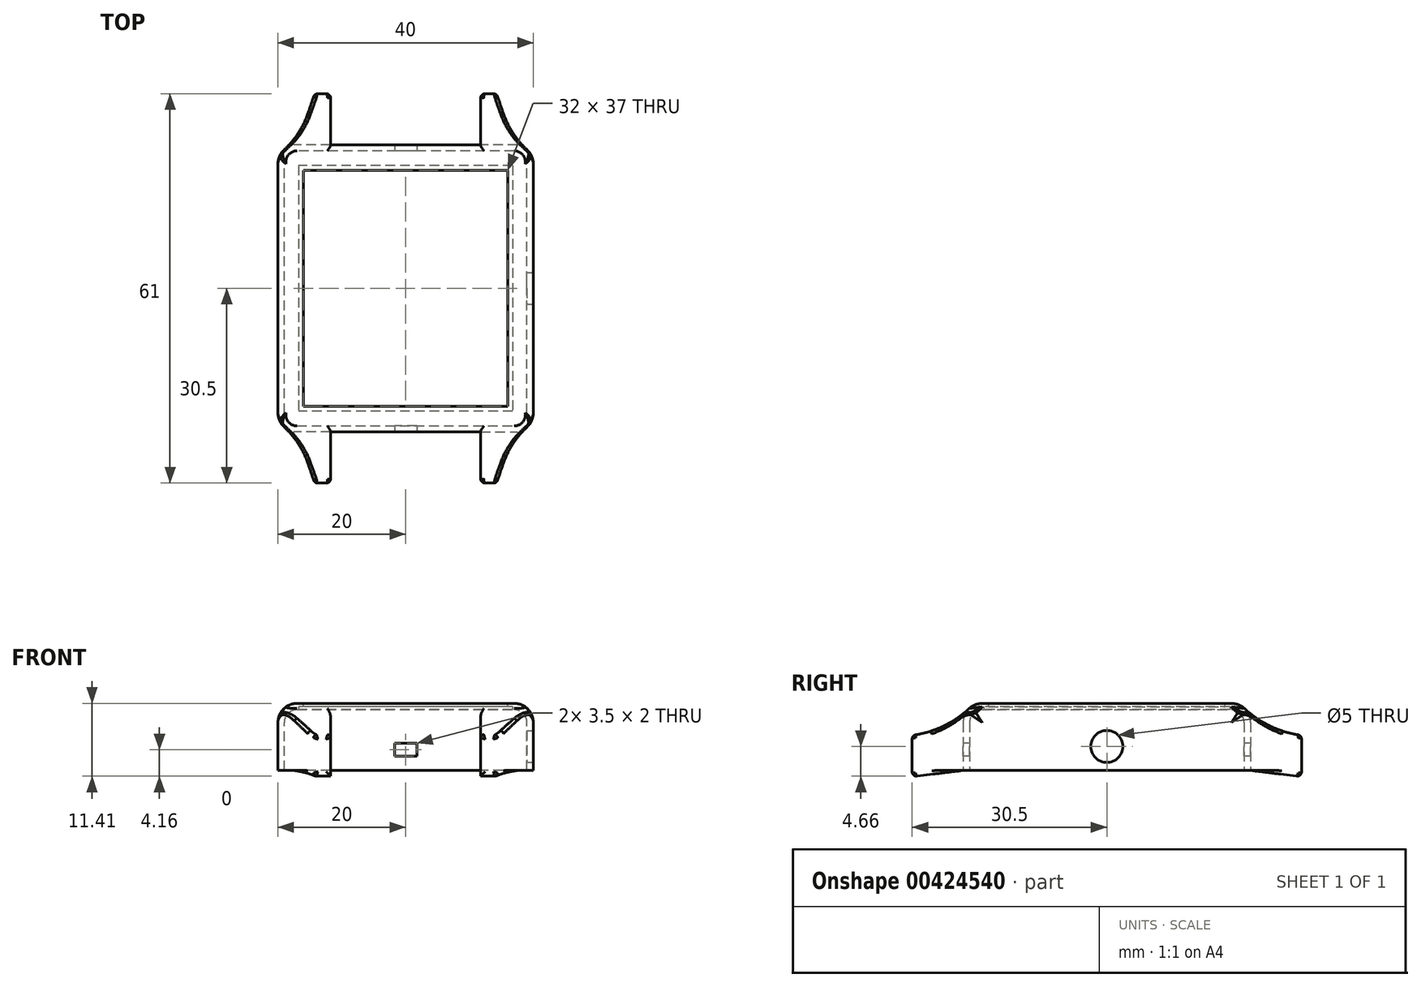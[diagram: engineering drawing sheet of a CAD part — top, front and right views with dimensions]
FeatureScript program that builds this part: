
annotation { "Feature Type Name" : "Feature", "Feature Type Description" : "" }
export const myFeature = defineFeature(function(context is Context, id is Id, definition is map)
    precondition{}
    {
        {
            var Q0;
            Q0=qCreatedBy(makeId("Top.planeOp"),FACE);
            var sketch = newSketch(context, id + "F0", { "sketchPlane" : qUnion([Q0])});
            skLineSegment(sketch, "E0.bottom", {"start": v(20, -22.5) * mm, "end": v(-20, -22.5) * mm});
            skLineSegment(sketch, "E0.top", {"start": v(20, 22.5) * mm, "end": v(-20, 22.5) * mm});
            skLineSegment(sketch, "E0.left", {"start": v(20, -22.5) * mm, "end": v(20, 22.5) * mm});
            skLineSegment(sketch, "E0.right", {"start": v(-20, -22.5) * mm, "end": v(-20, 22.5) * mm});
            skPoint(sketch, "E0.middle", {"position": v(0, 0) * mm});
            skSolve(sketch);
        }
        {
            var Q0;
            Q0=makeQuery(id+"F0.imprint","IMPRINT",FACE,{"disambiguationData":[TD([[makeQuery(id+"F0.imprint","IMPRINT",EDGE,{"derivedFrom":sQuery(id+"F0.wireOp",EDGE,"E0.bottom")}),-1.0]])]});
            extrude(context, id + "F1", {"entities" : qUnion([Q0]), "depth" : 10.5 * mm});
        }
        {
            var Q0;
            Q0=makeQuery(id+"F1.opExtrude","CAP_EDGE",EDGE,{"disambiguationData":[OSD([sQuery(id+"F0.wireOp",EDGE,"E0.bottom")])],"isStart":false});
            var Q1;
            Q1=makeQuery(id+"F1.opExtrude","CAP_EDGE",EDGE,{"disambiguationData":[OSD([sQuery(id+"F0.wireOp",EDGE,"E0.left")])],"isStart":false});
            var Q2;
            Q2=makeQuery(id+"F1.opExtrude","CAP_EDGE",EDGE,{"disambiguationData":[OSD([sQuery(id+"F0.wireOp",EDGE,"E0.right")])],"isStart":false});
            var Q3;
            Q3=makeQuery(id+"F1.opExtrude","CAP_EDGE",EDGE,{"disambiguationData":[OSD([sQuery(id+"F0.wireOp",EDGE,"E0.top")])],"isStart":false});
            var Q4;
            Q4=makeQuery(id+"F1.opExtrude","SWEPT_EDGE",EDGE,{"disambiguationData":[OSD([sQuery(id+"F0.wireOp",EDGE,"E0.top"),sQuery(id+"F0.wireOp",EDGE,"E0.left")])]});
            var Q5;
            Q5=makeQuery(id+"F1.opExtrude","SWEPT_EDGE",EDGE,{"disambiguationData":[OSD([sQuery(id+"F0.wireOp",EDGE,"E0.bottom"),sQuery(id+"F0.wireOp",EDGE,"E0.left")])]});
            var Q6;
            Q6=makeQuery(id+"F1.opExtrude","SWEPT_EDGE",EDGE,{"disambiguationData":[OSD([sQuery(id+"F0.wireOp",EDGE,"E0.bottom"),sQuery(id+"F0.wireOp",EDGE,"E0.right")])]});
            var Q7;
            Q7=makeQuery(id+"F1.opExtrude","SWEPT_EDGE",EDGE,{"disambiguationData":[OSD([sQuery(id+"F0.wireOp",EDGE,"E0.top"),sQuery(id+"F0.wireOp",EDGE,"E0.right")])]});
            fillet(context, id + "F2", {"entities" : qUnion([Q0, Q1, Q2, Q3, Q4, Q5, Q6, Q7]), "radius" : 3 * mm, "tangentPropagation" : true, "allowEdgeOverflow" : false});
        }
        {
            var Q0;
            Q0=makeQuery(id+"F1.opExtrude","CAP_FACE",FACE,{"disambiguationData":[OSD([sQuery(id+"F0.wireOp",EDGE,"E0.bottom"),sQuery(id+"F0.wireOp",EDGE,"E0.top"),sQuery(id+"F0.wireOp",EDGE,"E0.left"),sQuery(id+"F0.wireOp",EDGE,"E0.right")])],"isStart":true});
            shell(context, id + "F3", {"entities" : qUnion([Q0]), "thickness" : 1 * mm});
        }
        {
            var Q0;
            Q0=makeQuery(id+"F1.opExtrude","CAP_FACE",FACE,{"disambiguationData":[OSD([sQuery(id+"F0.wireOp",EDGE,"E0.bottom"),sQuery(id+"F0.wireOp",EDGE,"E0.top"),sQuery(id+"F0.wireOp",EDGE,"E0.left"),sQuery(id+"F0.wireOp",EDGE,"E0.right")])],"isStart":true});
            var sketch = newSketch(context, id + "F4", { "sketchPlane" : qUnion([Q0])});
            skLineSegment(sketch, "E1", {"start": v(0, 22.5) * mm, "end": v(0, -22.5) * mm});
            skLineSegment(sketch, "E2", {"start": v(-20, 0) * mm, "end": v(20, 0) * mm});
            skLineSegment(sketch, "E3", {"start": v(-17, 22.5) * mm, "end": v(-17, -22.5) * mm});
            skLineSegment(sketch, "E4", {"start": v(17, 22.5) * mm, "end": v(17, -22.5) * mm});
            skLineSegment(sketch, "E5", {"start": v(-11.75, 22.5) * mm, "end": v(-11.75, -22.5) * mm});
            skLineSegment(sketch, "E6", {"start": v(11.75, 22.5) * mm, "end": v(11.75, -22.5) * mm});
            skLineSegment(sketch, "E7", {"start": v(-11.75, -22.5) * mm, "end": v(-11.75, -30.5) * mm});
            skLineSegment(sketch, "E8", {"start": v(11.75, -22.5) * mm, "end": v(11.75, -30.5) * mm});
            skLineSegment(sketch, "E9", {"start": v(-11.75, -30.5) * mm, "end": v(-14.25, -30.5) * mm});
            skLineSegment(sketch, "E10", {"start": v(-14.25, -30.5) * mm, "end": v(-17, -22.5) * mm});
            skLineSegment(sketch, "E11", {"start": v(11.75, -30.5) * mm, "end": v(14.25, -30.5) * mm});
            skLineSegment(sketch, "E12", {"start": v(14.25, -30.5) * mm, "end": v(17, -22.5) * mm});
            skLineSegment(sketch, "E13", {"start": v(-11.75, 22.5) * mm, "end": v(-11.75, 30.5) * mm});
            skLineSegment(sketch, "E14", {"start": v(11.75, 22.5) * mm, "end": v(11.75, 30.5) * mm});
            skLineSegment(sketch, "E15", {"start": v(11.75, 30.5) * mm, "end": v(14.25, 30.5) * mm});
            skLineSegment(sketch, "E16", {"start": v(14.25, 30.5) * mm, "end": v(17, 22.5) * mm});
            skLineSegment(sketch, "E17", {"start": v(-11.75, 30.5) * mm, "end": v(-14.25, 30.5) * mm});
            skLineSegment(sketch, "E18", {"start": v(-14.25, 30.5) * mm, "end": v(-17, 22.5) * mm});
            skSolve(sketch);
        }
        {
            var Q0;
            {var subQ0=sQuery(id+"F4.wireOp",EDGE,"E13");Q0=makeQuery(id+"F4.imprint","IMPRINT",FACE,{"disambiguationData":[TD([[makeQuery(id+"F4.imprint","IMPRINT",EDGE,{"derivedFrom":subQ0}),1.0]])]});}
            var Q1;
            {var subQ0=sQuery(id+"F4.wireOp",EDGE,"E14");Q1=makeQuery(id+"F4.imprint","IMPRINT",FACE,{"disambiguationData":[TD([[makeQuery(id+"F4.imprint","IMPRINT",EDGE,{"derivedFrom":subQ0}),-1.0]])]});}
            var Q2;
            {var subQ0=sQuery(id+"F4.wireOp",EDGE,"E8");Q2=makeQuery(id+"F4.imprint","IMPRINT",FACE,{"disambiguationData":[TD([[makeQuery(id+"F4.imprint","IMPRINT",EDGE,{"derivedFrom":subQ0}),1.0]])]});}
            var Q3;
            {var subQ0=sQuery(id+"F4.wireOp",EDGE,"E7");Q3=makeQuery(id+"F4.imprint","IMPRINT",FACE,{"disambiguationData":[TD([[makeQuery(id+"F4.imprint","IMPRINT",EDGE,{"derivedFrom":subQ0}),-1.0]])]});}
            extrude(context, id + "F5", {"entities" : qUnion([Q0, Q1, Q2, Q3]), "operationType" : NewBodyOperationType.ADD, "oppositeDirection" : true, "depth" : 6.5 * mm});
        }
        {
            var Q0;
            {var subQ0=sQuery(id+"F4.wireOp",EDGE,"E13");Q0=makeQuery(id+"F4.imprint","IMPRINT",FACE,{"disambiguationData":[TD([[makeQuery(id+"F4.imprint","IMPRINT",EDGE,{"derivedFrom":subQ0}),1.0]])]});}
            extrude(context, id + "F6", {"entities" : qUnion([Q0]), "operationType" : NewBodyOperationType.ADD, "depth" : 1 * mm});
        }
        {
            var Q0;
            Q0=makeQuery(id+"F5.opExtrude","CAP_EDGE",EDGE,{"disambiguationData":[OSD([sQuery(id+"F4.wireOp",EDGE,"E17")])],"isStart":false});
            chamfer(context, id + "F7", {"entities" : qUnion([Q0]), "chamferType" : ChamferType.TWO_OFFSETS, "width1" : 1 * mm, "oppositeDirection" : false, "width2" : 8 * mm, "tangentPropagation" : true});
        }
        {
            var Q0;
            {var subQ0=sQuery(id+"F0.wireOp",EDGE,"E0.bottom");var subQ1=sQuery(id+"F0.wireOp",EDGE,"E0.top");Q0=makeQuery(id+"F5.boolean.opBoolean","MERGE",FACE,{"derivedFrom":[makeQuery(id+"F1.opExtrude","CAP_FACE",FACE,{"disambiguationData":[OSD([subQ0,subQ1,sQuery(id+"F0.wireOp",EDGE,"E0.left"),sQuery(id+"F0.wireOp",EDGE,"E0.right")])],"isStart":true}),makeQuery(id+"F5.opExtrude","CAP_FACE",FACE,{"disambiguationData":[OSD([subQ1,sQuery(id+"F4.wireOp",EDGE,"E7"),sQuery(id+"F4.wireOp",EDGE,"E9"),sQuery(id+"F4.wireOp",EDGE,"E10")])],"isStart":true}),makeQuery(id+"F5.opExtrude","CAP_FACE",FACE,{"disambiguationData":[OSD([subQ1,sQuery(id+"F4.wireOp",EDGE,"E8"),sQuery(id+"F4.wireOp",EDGE,"E11"),sQuery(id+"F4.wireOp",EDGE,"E12")])],"isStart":true}),makeQuery(id+"F5.opExtrude","CAP_FACE",FACE,{"disambiguationData":[OSD([subQ0,sQuery(id+"F4.wireOp",EDGE,"E13"),sQuery(id+"F4.wireOp",EDGE,"E17"),sQuery(id+"F4.wireOp",EDGE,"E18")])],"isStart":true}),makeQuery(id+"F5.opExtrude","CAP_FACE",FACE,{"disambiguationData":[OSD([subQ0,sQuery(id+"F4.wireOp",EDGE,"E14"),sQuery(id+"F4.wireOp",EDGE,"E15"),sQuery(id+"F4.wireOp",EDGE,"E16")])],"isStart":true})]});}
            var sketch = newSketch(context, id + "F8", { "sketchPlane" : qUnion([Q0])});
            skLineSegment(sketch, "E19", {"start": v(11.75, 22.5) * mm, "end": v(17, 22.5) * mm});
            skLineSegment(sketch, "E20", {"start": v(-11.75, -22.5) * mm, "end": v(-17, -22.5) * mm});
            skLineSegment(sketch, "E21", {"start": v(17, -22.5) * mm, "end": v(11.75, -22.5) * mm});
            skSolve(sketch);
        }
        {
            var Q0;
            Q0=makeQuery(id+"F8.imprint","IMPRINT",FACE,{"disambiguationData":[TD([[makeQuery(id+"F8.imprint","IMPRINT",EDGE,{"derivedFrom":sQuery(id+"F8.wireOp",EDGE,"E21")}),1.0]])]});
            var Q1;
            Q1=makeQuery(id+"F8.imprint","IMPRINT",FACE,{"disambiguationData":[TD([[makeQuery(id+"F8.imprint","IMPRINT",EDGE,{"derivedFrom":sQuery(id+"F8.wireOp",EDGE,"E20")}),1.0]])]});
            var Q2;
            Q2=makeQuery(id+"F8.imprint","IMPRINT",FACE,{"disambiguationData":[TD([[makeQuery(id+"F8.imprint","IMPRINT",EDGE,{"derivedFrom":sQuery(id+"F8.wireOp",EDGE,"E19")}),1.0]])]});
            extrude(context, id + "F9", {"entities" : qUnion([Q0, Q1, Q2]), "operationType" : NewBodyOperationType.ADD, "depth" : 1 * mm});
        }
        {
            var Q0;
            Q0=makeQuery(id+"F6.opExtrude","CAP_EDGE",EDGE,{"disambiguationData":[OSD([sQuery(id+"F0.wireOp",EDGE,"E0.bottom")])],"isStart":false});
            chamfer(context, id + "F10", {"entities" : qUnion([Q0]), "chamferType" : ChamferType.TWO_OFFSETS, "width1" : 1 * mm, "oppositeDirection" : false, "width2" : 8 * mm, "tangentPropagation" : true});
        }
        {
            var Q0;
            Q0=makeQuery(id+"F9.opExtrude","CAP_EDGE",EDGE,{"disambiguationData":[OSD([sQuery(id+"F8.wireOp",EDGE,"E21")])],"isStart":false});
            var Q1;
            Q1=makeQuery(id+"F9.opExtrude","CAP_EDGE",EDGE,{"disambiguationData":[OSD([sQuery(id+"F8.wireOp",EDGE,"E20")])],"isStart":false});
            chamfer(context, id + "F11", {"entities" : qUnion([Q0, Q1]), "chamferType" : ChamferType.TWO_OFFSETS, "width1" : 8 * mm, "oppositeDirection" : false, "width2" : 1 * mm, "tangentPropagation" : true});
        }
        {
            var Q0;
            Q0=makeQuery(id+"F9.opExtrude","CAP_EDGE",EDGE,{"disambiguationData":[OSD([sQuery(id+"F8.wireOp",EDGE,"E19")])],"isStart":false});
            chamfer(context, id + "F12", {"entities" : qUnion([Q0]), "chamferType" : ChamferType.TWO_OFFSETS, "width1" : 1 * mm, "oppositeDirection" : true, "width2" : 8 * mm, "tangentPropagation" : true});
        }
        {
            var Q0;
            Q0=makeQuery(id+"F5.opExtrude","CAP_EDGE",EDGE,{"disambiguationData":[OSD([sQuery(id+"F4.wireOp",EDGE,"E11")])],"isStart":false});
            chamfer(context, id + "F13", {"entities" : qUnion([Q0]), "chamferType" : ChamferType.TWO_OFFSETS, "width1" : 1 * mm, "oppositeDirection" : false, "width2" : 8 * mm});
        }
        {
            var Q0;
            Q0=makeQuery(id+"F5.opExtrude","CAP_EDGE",EDGE,{"disambiguationData":[OSD([sQuery(id+"F4.wireOp",EDGE,"E15")])],"isStart":false});
            chamfer(context, id + "F14", {"entities" : qUnion([Q0]), "chamferType" : ChamferType.TWO_OFFSETS, "width1" : 1 * mm, "oppositeDirection" : true, "width2" : 8 * mm, "tangentPropagation" : true});
        }
        {
            var Q0;
            Q0=makeQuery(id+"F5.opExtrude","CAP_EDGE",EDGE,{"disambiguationData":[OSD([sQuery(id+"F4.wireOp",EDGE,"E9")])],"isStart":false});
            chamfer(context, id + "F15", {"entities" : qUnion([Q0]), "chamferType" : ChamferType.TWO_OFFSETS, "width1" : 1 * mm, "oppositeDirection" : true, "width2" : 8 * mm, "tangentPropagation" : true});
        }
        {
            var Q0;
            Q0=makeQuery(id+"F1.opExtrude","SWEPT_FACE",FACE,{"disambiguationData":[OSD([sQuery(id+"F0.wireOp",EDGE,"E0.bottom")])]});
            var sketch = newSketch(context, id + "F16", { "sketchPlane" : qUnion([Q0])});
            skLineSegment(sketch, "E22", {"start": v(-11.75, 3.25) * mm, "end": v(11.75, 3.25) * mm});
            skLineSegment(sketch, "E23", {"start": v(0, 0) * mm, "end": v(0, 7.5) * mm});
            skLineSegment(sketch, "E24.bottom", {"start": v(1.75, 2.25) * mm, "end": v(-1.75, 2.25) * mm});
            skLineSegment(sketch, "E24.top", {"start": v(1.75, 4.25) * mm, "end": v(-1.75, 4.25) * mm});
            skLineSegment(sketch, "E24.left", {"start": v(1.75, 2.25) * mm, "end": v(1.75, 4.25) * mm});
            skLineSegment(sketch, "E24.right", {"start": v(-1.75, 2.25) * mm, "end": v(-1.75, 4.25) * mm});
            skPoint(sketch, "E24.middle", {"position": v(0, 3.25) * mm});
            skSolve(sketch);
        }
        {
            var Q0;
            {var subQ0=sQuery(id+"F16.wireOp",EDGE,"E24.right");var subQ1=sQuery(id+"F16.wireOp",EDGE,"E22");var subQ2=makeQuery(id+"F16.imprint","INTERSECT",VERTEX,{"derivedFrom":[subQ1,subQ0]});Q0=makeQuery(id+"F16.imprint","IMPRINT",FACE,{"disambiguationData":[TD([[makeQuery(id+"F16.imprint","IMPRINT",EDGE,{"disambiguationData":[TD([[subQ2,-1.0]])],"derivedFrom":subQ1}),1.0]])]});}
            var Q1;
            {var subQ0=sQuery(id+"F16.wireOp",EDGE,"E23");var subQ1=sQuery(id+"F16.wireOp",EDGE,"E22");var subQ2=makeQuery(id+"F16.imprint","INTERSECT",VERTEX,{"derivedFrom":[subQ1,subQ0]});Q1=makeQuery(id+"F16.imprint","IMPRINT",FACE,{"disambiguationData":[TD([[makeQuery(id+"F16.imprint","IMPRINT",EDGE,{"disambiguationData":[TD([[subQ2,-1.0]])],"derivedFrom":subQ1}),1.0]])]});}
            var Q2;
            {var subQ0=sQuery(id+"F16.wireOp",EDGE,"E23");var subQ1=sQuery(id+"F16.wireOp",EDGE,"E22");var subQ2=makeQuery(id+"F16.imprint","INTERSECT",VERTEX,{"derivedFrom":[subQ1,subQ0]});Q2=makeQuery(id+"F16.imprint","IMPRINT",FACE,{"disambiguationData":[TD([[makeQuery(id+"F16.imprint","IMPRINT",EDGE,{"disambiguationData":[TD([[subQ2,-1.0]])],"derivedFrom":subQ1}),-1.0]])]});}
            var Q3;
            {var subQ0=sQuery(id+"F16.wireOp",EDGE,"E24.right");var subQ1=sQuery(id+"F16.wireOp",EDGE,"E22");var subQ2=makeQuery(id+"F16.imprint","INTERSECT",VERTEX,{"derivedFrom":[subQ1,subQ0]});Q3=makeQuery(id+"F16.imprint","IMPRINT",FACE,{"disambiguationData":[TD([[makeQuery(id+"F16.imprint","IMPRINT",EDGE,{"disambiguationData":[TD([[subQ2,-1.0]])],"derivedFrom":subQ1}),-1.0]])]});}
            extrude(context, id + "F17", {"entities" : qUnion([Q0, Q1, Q2, Q3]), "operationType" : NewBodyOperationType.REMOVE, "oppositeDirection" : true, "depth" : 50 * mm});
        }
        {
            var Q0;
            Q0=makeQuery(id+"F1.opExtrude","SWEPT_FACE",FACE,{"disambiguationData":[OSD([sQuery(id+"F0.wireOp",EDGE,"E0.left")])]});
            var sketch = newSketch(context, id + "F18", { "sketchPlane" : qUnion([Q0])});
            skLineSegment(sketch, "E25", {"start": v(19.5, 3.75) * mm, "end": v(-19.5, 3.75) * mm});
            skLineSegment(sketch, "E26", {"start": v(0, 7.5) * mm, "end": v(0, 0) * mm});
            skCircle(sketch, "E27", {"center": v(0, 3.75) * mm, "radius": 2.5 * mm});
            skSolve(sketch);
        }
        {
            var Q0;
            {var subQ0=sQuery(id+"F18.wireOp",EDGE,"E26");var subQ1=sQuery(id+"F18.wireOp",EDGE,"E25");var subQ2=makeQuery(id+"F18.imprint","INTERSECT",VERTEX,{"derivedFrom":[subQ1,subQ0]});Q0=makeQuery(id+"F18.imprint","IMPRINT",FACE,{"disambiguationData":[TD([[makeQuery(id+"F18.imprint","IMPRINT",EDGE,{"disambiguationData":[TD([[subQ2,-1.0]])],"derivedFrom":subQ1}),-1.0]])]});}
            var Q1;
            {var subQ0=sQuery(id+"F18.wireOp",EDGE,"E27");var subQ1=sQuery(id+"F18.wireOp",EDGE,"E25");var subQ2=makeQuery(id+"F18.imprint","INTERSECT",VERTEX,{"disambiguationData":[OD(0.0)],"derivedFrom":[subQ1,subQ0]});Q1=makeQuery(id+"F18.imprint","IMPRINT",FACE,{"disambiguationData":[TD([[makeQuery(id+"F18.imprint","IMPRINT",EDGE,{"disambiguationData":[TD([[subQ2,-1.0]])],"derivedFrom":subQ1}),-1.0]])]});}
            var Q2;
            {var subQ0=sQuery(id+"F18.wireOp",EDGE,"E27");var subQ1=sQuery(id+"F18.wireOp",EDGE,"E25");var subQ2=makeQuery(id+"F18.imprint","INTERSECT",VERTEX,{"disambiguationData":[OD(0.0)],"derivedFrom":[subQ1,subQ0]});Q2=makeQuery(id+"F18.imprint","IMPRINT",FACE,{"disambiguationData":[TD([[makeQuery(id+"F18.imprint","IMPRINT",EDGE,{"disambiguationData":[TD([[subQ2,-1.0]])],"derivedFrom":subQ1}),1.0]])]});}
            var Q3;
            {var subQ0=sQuery(id+"F18.wireOp",EDGE,"E26");var subQ1=sQuery(id+"F18.wireOp",EDGE,"E25");var subQ2=makeQuery(id+"F18.imprint","INTERSECT",VERTEX,{"derivedFrom":[subQ1,subQ0]});Q3=makeQuery(id+"F18.imprint","IMPRINT",FACE,{"disambiguationData":[TD([[makeQuery(id+"F18.imprint","IMPRINT",EDGE,{"disambiguationData":[TD([[subQ2,-1.0]])],"derivedFrom":subQ1}),1.0]])]});}
            extrude(context, id + "F19", {"entities" : qUnion([Q0, Q1, Q2, Q3]), "operationType" : NewBodyOperationType.REMOVE, "oppositeDirection" : true, "depth" : 10 * mm});
        }
        {
            var Q0;
            Q0=makeQuery(id+"F1.opExtrude","CAP_FACE",FACE,{"disambiguationData":[OSD([sQuery(id+"F0.wireOp",EDGE,"E0.bottom"),sQuery(id+"F0.wireOp",EDGE,"E0.top"),sQuery(id+"F0.wireOp",EDGE,"E0.left"),sQuery(id+"F0.wireOp",EDGE,"E0.right")])],"isStart":false});
            var sketch = newSketch(context, id + "F20", { "sketchPlane" : qUnion([Q0])});
            skLineSegment(sketch, "E28.bottom", {"start": v(16, -18.5) * mm, "end": v(-16, -18.5) * mm});
            skLineSegment(sketch, "E28.top", {"start": v(16, 18.5) * mm, "end": v(-16, 18.5) * mm});
            skLineSegment(sketch, "E28.left", {"start": v(16, -18.5) * mm, "end": v(16, 18.5) * mm});
            skLineSegment(sketch, "E28.right", {"start": v(-16, -18.5) * mm, "end": v(-16, 18.5) * mm});
            skPoint(sketch, "E28.middle", {"position": v(0, 0) * mm});
            skSolve(sketch);
        }
        {
            var Q0;
            Q0=makeQuery(id+"F20.imprint","IMPRINT",FACE,{"disambiguationData":[TD([[makeQuery(id+"F20.imprint","IMPRINT",EDGE,{"derivedFrom":sQuery(id+"F20.wireOp",EDGE,"E28.bottom")}),-1.0]])]});
            extrude(context, id + "F21", {"entities" : qUnion([Q0]), "operationType" : NewBodyOperationType.REMOVE, "oppositeDirection" : true, "depth" : 25 * mm});
        }
        {
            var Q0;
            Q0=makeQuery(id+"F3.opShell","OFFSET_FACE",FACE,{"disambiguationData":[OSD([sQuery(id+"F0.wireOp",EDGE,"E0.bottom"),sQuery(id+"F0.wireOp",EDGE,"E0.top"),sQuery(id+"F0.wireOp",EDGE,"E0.left"),sQuery(id+"F0.wireOp",EDGE,"E0.right")])]});
            var sketch = newSketch(context, id + "F22", { "sketchPlane" : qUnion([Q0])});
            skLineSegment(sketch, "E29.bottom", {"start": v(16.75, -19.25) * mm, "end": v(-16.75, -19.25) * mm});
            skLineSegment(sketch, "E29.top", {"start": v(16.75, 19.25) * mm, "end": v(-16.75, 19.25) * mm});
            skLineSegment(sketch, "E29.left", {"start": v(16.75, -19.25) * mm, "end": v(16.75, 19.25) * mm});
            skLineSegment(sketch, "E29.right", {"start": v(-16.75, -19.25) * mm, "end": v(-16.75, 19.25) * mm});
            skPoint(sketch, "E29.middle", {"position": v(0, 0) * mm});
            skSolve(sketch);
        }
        {
            var Q0;
            Q0=makeQuery(id+"F22.imprint","IMPRINT",FACE,{"disambiguationData":[TD([[makeQuery(id+"F22.imprint","IMPRINT",EDGE,{"derivedFrom":sQuery(id+"F22.wireOp",EDGE,"E29.bottom")}),-1.0]])]});
            extrude(context, id + "F23", {"entities" : qUnion([Q0]), "operationType" : NewBodyOperationType.REMOVE, "oppositeDirection" : true, "depth" : .5 * mm});
        }
        {
            var Q0;
            {var subQ0=sQuery(id+"F0.wireOp",EDGE,"E0.right");var subQ1=sQuery(id+"F0.wireOp",EDGE,"E0.bottom");Q0=makeQuery(id+"F5.boolean.opBoolean","MERGE",EDGE,{"derivedFrom":[makeQuery(id+"F2.opFillet","BLEND_EDGE",EDGE,{"blendedFrom":[makeQuery(id+"F1.opExtrude","SWEPT_EDGE",EDGE,{"disambiguationData":[OSD([subQ1,subQ0])]}),makeQuery(id+"F1.opExtrude","SWEPT_FACE",FACE,{"disambiguationData":[OSD([subQ1])]})],"blendedInto":[makeQuery(id+"F1.opExtrude","SWEPT_FACE",FACE,{"disambiguationData":[OSD([subQ1])]})]}),makeQuery(id+"F5.opExtrude","SWEPT_EDGE",EDGE,{"disambiguationData":[OSD([subQ1,sQuery(id+"F0.wireOp",EDGE,"E0.top"),sQuery(id+"F0.wireOp",EDGE,"E0.left"),subQ0,sQuery(id+"F4.wireOp",EDGE,"E3"),sQuery(id+"F4.wireOp",EDGE,"E18")])]})]});}
            var Q1;
            {var subQ0=sQuery(id+"F0.wireOp",EDGE,"E0.left");var subQ1=sQuery(id+"F0.wireOp",EDGE,"E0.bottom");Q1=makeQuery(id+"F5.boolean.opBoolean","MERGE",EDGE,{"derivedFrom":[makeQuery(id+"F2.opFillet","BLEND_EDGE",EDGE,{"blendedFrom":[makeQuery(id+"F1.opExtrude","SWEPT_EDGE",EDGE,{"disambiguationData":[OSD([subQ1,subQ0])]}),makeQuery(id+"F1.opExtrude","SWEPT_FACE",FACE,{"disambiguationData":[OSD([subQ1])]})],"blendedInto":[makeQuery(id+"F1.opExtrude","SWEPT_FACE",FACE,{"disambiguationData":[OSD([subQ1])]})]}),makeQuery(id+"F5.opExtrude","SWEPT_EDGE",EDGE,{"disambiguationData":[OSD([subQ1,sQuery(id+"F0.wireOp",EDGE,"E0.top"),subQ0,sQuery(id+"F0.wireOp",EDGE,"E0.right"),sQuery(id+"F4.wireOp",EDGE,"E4"),sQuery(id+"F4.wireOp",EDGE,"E16")])]})]});}
            var Q2;
            {var subQ0=sQuery(id+"F0.wireOp",EDGE,"E0.right");var subQ1=sQuery(id+"F0.wireOp",EDGE,"E0.top");Q2=makeQuery(id+"F5.boolean.opBoolean","MERGE",EDGE,{"derivedFrom":[makeQuery(id+"F2.opFillet","BLEND_EDGE",EDGE,{"blendedFrom":[makeQuery(id+"F1.opExtrude","SWEPT_EDGE",EDGE,{"disambiguationData":[OSD([subQ1,subQ0])]}),makeQuery(id+"F1.opExtrude","SWEPT_FACE",FACE,{"disambiguationData":[OSD([subQ1])]})],"blendedInto":[makeQuery(id+"F1.opExtrude","SWEPT_FACE",FACE,{"disambiguationData":[OSD([subQ1])]})]}),makeQuery(id+"F5.opExtrude","SWEPT_EDGE",EDGE,{"disambiguationData":[OSD([sQuery(id+"F0.wireOp",EDGE,"E0.bottom"),subQ1,sQuery(id+"F0.wireOp",EDGE,"E0.left"),subQ0,sQuery(id+"F4.wireOp",EDGE,"E3"),sQuery(id+"F4.wireOp",EDGE,"E10")])]})]});}
            var Q3;
            {var subQ0=sQuery(id+"F0.wireOp",EDGE,"E0.left");var subQ1=sQuery(id+"F0.wireOp",EDGE,"E0.top");Q3=makeQuery(id+"F5.boolean.opBoolean","MERGE",EDGE,{"derivedFrom":[makeQuery(id+"F2.opFillet","BLEND_EDGE",EDGE,{"blendedFrom":[makeQuery(id+"F1.opExtrude","SWEPT_EDGE",EDGE,{"disambiguationData":[OSD([subQ1,subQ0])]}),makeQuery(id+"F1.opExtrude","SWEPT_FACE",FACE,{"disambiguationData":[OSD([subQ1])]})],"blendedInto":[makeQuery(id+"F1.opExtrude","SWEPT_FACE",FACE,{"disambiguationData":[OSD([subQ1])]})]}),makeQuery(id+"F5.opExtrude","SWEPT_EDGE",EDGE,{"disambiguationData":[OSD([sQuery(id+"F0.wireOp",EDGE,"E0.bottom"),subQ1,subQ0,sQuery(id+"F0.wireOp",EDGE,"E0.right"),sQuery(id+"F4.wireOp",EDGE,"E4"),sQuery(id+"F4.wireOp",EDGE,"E12")])]})]});}
            fillet(context, id + "F24", {"entities" : qUnion([Q0, Q1, Q2, Q3]), "radius" : 14 * mm, "tangentPropagation" : true, "allowEdgeOverflow" : false});
        }
        {
            var Q0;
            Q0=makeQuery(id+"F13.opChamfer","BLEND_EDGE",EDGE,{"blendedFrom":[makeQuery(id+"F5.opExtrude","CAP_EDGE",EDGE,{"disambiguationData":[OSD([sQuery(id+"F4.wireOp",EDGE,"E11")])],"isStart":false}),makeQuery(id+"F1.opExtrude","SWEPT_FACE",FACE,{"disambiguationData":[OSD([sQuery(id+"F0.wireOp",EDGE,"E0.top")])]})],"blendedInto":[makeQuery(id+"F1.opExtrude","SWEPT_FACE",FACE,{"disambiguationData":[OSD([sQuery(id+"F0.wireOp",EDGE,"E0.top")])]})]});
            var Q1;
            Q1=makeQuery(id+"F14.opChamfer","BLEND_EDGE",EDGE,{"blendedFrom":[makeQuery(id+"F5.opExtrude","CAP_EDGE",EDGE,{"disambiguationData":[OSD([sQuery(id+"F4.wireOp",EDGE,"E15")])],"isStart":false}),makeQuery(id+"F1.opExtrude","SWEPT_FACE",FACE,{"disambiguationData":[OSD([sQuery(id+"F0.wireOp",EDGE,"E0.bottom")])]})],"blendedInto":[makeQuery(id+"F1.opExtrude","SWEPT_FACE",FACE,{"disambiguationData":[OSD([sQuery(id+"F0.wireOp",EDGE,"E0.bottom")])]})]});
            var Q2;
            Q2=makeQuery(id+"F7.opChamfer","BLEND_EDGE",EDGE,{"blendedFrom":[makeQuery(id+"F5.opExtrude","CAP_EDGE",EDGE,{"disambiguationData":[OSD([sQuery(id+"F4.wireOp",EDGE,"E17")])],"isStart":false}),makeQuery(id+"F1.opExtrude","SWEPT_FACE",FACE,{"disambiguationData":[OSD([sQuery(id+"F0.wireOp",EDGE,"E0.bottom")])]})],"blendedInto":[makeQuery(id+"F1.opExtrude","SWEPT_FACE",FACE,{"disambiguationData":[OSD([sQuery(id+"F0.wireOp",EDGE,"E0.bottom")])]})]});
            var Q3;
            Q3=makeQuery(id+"F15.opChamfer","BLEND_EDGE",EDGE,{"blendedFrom":[makeQuery(id+"F5.opExtrude","CAP_EDGE",EDGE,{"disambiguationData":[OSD([sQuery(id+"F4.wireOp",EDGE,"E9")])],"isStart":false}),makeQuery(id+"F1.opExtrude","SWEPT_FACE",FACE,{"disambiguationData":[OSD([sQuery(id+"F0.wireOp",EDGE,"E0.top")])]})],"blendedInto":[makeQuery(id+"F1.opExtrude","SWEPT_FACE",FACE,{"disambiguationData":[OSD([sQuery(id+"F0.wireOp",EDGE,"E0.top")])]})]});
            var Q4;
            {var subQ0=sQuery(id+"F4.wireOp",EDGE,"E10");var subQ1=sQuery(id+"F0.wireOp",EDGE,"E0.top");var subQ2=sQuery(id+"F0.wireOp",EDGE,"E0.right");Q4=makeQuery(id+"F24.opFillet","TWEAK_EDGE",EDGE,{"derivedFrom":[makeQuery(id+"F15.opChamfer","BLEND_VERTEX",VERTEX,{"blendedFrom":[makeQuery(id+"F5.opExtrude","CAP_EDGE",EDGE,{"disambiguationData":[OSD([sQuery(id+"F4.wireOp",EDGE,"E9")])],"isStart":false}),makeQuery(id+"F2.opFillet","BLEND_FACE",FACE,{"disambiguationData":[OSD([subQ1,subQ2]),TDD([makeQuery(id+"F1.opExtrude","SWEPT_EDGE",EDGE,{"disambiguationData":[OSD([subQ1,subQ2])]})])]}),makeQuery(id+"F1.opExtrude","SWEPT_FACE",FACE,{"disambiguationData":[OSD([subQ1])]}),makeQuery(id+"F9.boolean.opBoolean","MERGE",FACE,{"derivedFrom":[makeQuery(id+"F5.opExtrude","SWEPT_FACE",FACE,{"disambiguationData":[OSD([subQ0])]}),makeQuery(id+"F9.opExtrude","SWEPT_FACE",FACE,{"disambiguationData":[OSD([subQ0])]})]})],"blendedInto":[makeQuery(id+"F2.opFillet","BLEND_FACE",FACE,{"disambiguationData":[OSD([subQ1,subQ2]),TDD([makeQuery(id+"F1.opExtrude","SWEPT_EDGE",EDGE,{"disambiguationData":[OSD([subQ1,subQ2])]})])]}),makeQuery(id+"F1.opExtrude","SWEPT_FACE",FACE,{"disambiguationData":[OSD([subQ1])]}),makeQuery(id+"F9.boolean.opBoolean","MERGE",FACE,{"derivedFrom":[makeQuery(id+"F5.opExtrude","SWEPT_FACE",FACE,{"disambiguationData":[OSD([subQ0])]}),makeQuery(id+"F9.opExtrude","SWEPT_FACE",FACE,{"disambiguationData":[OSD([subQ0])]})]})]})]});}
            fillet(context, id + "F25", {"entities" : qUnion([Q0, Q1, Q2, Q3, Q4]), "radius" : 16 * mm, "tangentPropagation" : true, "allowEdgeOverflow" : false});
        }
        {
            var Q0;
            {var subQ0=sQuery(id+"F0.wireOp",EDGE,"E0.right");var subQ1=sQuery(id+"F0.wireOp",EDGE,"E0.top");Q0=makeQuery(id+"F25.opFillet","TWEAK_EDGE",EDGE,{"derivedFrom":[makeQuery(id+"F2.opFillet","BLEND_VERTEX",VERTEX,{"blendedFrom":[makeQuery(id+"F1.opExtrude","CAP_VERTEX",VERTEX,{"disambiguationData":[OSD([subQ1,subQ0])],"isStart":false}),makeQuery(id+"F1.opExtrude","SWEPT_EDGE",EDGE,{"disambiguationData":[OSD([subQ1,subQ0])]}),makeQuery(id+"F1.opExtrude","CAP_EDGE",EDGE,{"disambiguationData":[OSD([subQ0])],"isStart":false}),makeQuery(id+"F1.opExtrude","SWEPT_FACE",FACE,{"disambiguationData":[OSD([subQ0])]})],"blendedInto":[makeQuery(id+"F1.opExtrude","SWEPT_FACE",FACE,{"disambiguationData":[OSD([subQ0])]})]})]});}
            var Q1;
            Q1=makeQuery(id+"F25.opFillet","BLEND_EDGE",EDGE,{"blendedFrom":[makeQuery(id+"F15.opChamfer","BLEND_EDGE",EDGE,{"blendedFrom":[makeQuery(id+"F5.opExtrude","CAP_EDGE",EDGE,{"disambiguationData":[OSD([sQuery(id+"F4.wireOp",EDGE,"E9")])],"isStart":false}),makeQuery(id+"F1.opExtrude","SWEPT_FACE",FACE,{"disambiguationData":[OSD([sQuery(id+"F0.wireOp",EDGE,"E0.top")])]})],"blendedInto":[makeQuery(id+"F1.opExtrude","SWEPT_FACE",FACE,{"disambiguationData":[OSD([sQuery(id+"F0.wireOp",EDGE,"E0.top")])]})]}),makeQuery(id+"F2.opFillet","BLEND_FACE",FACE,{"disambiguationData":[OSD([sQuery(id+"F0.wireOp",EDGE,"E0.right")])]})],"blendedInto":[makeQuery(id+"F2.opFillet","BLEND_FACE",FACE,{"disambiguationData":[OSD([sQuery(id+"F0.wireOp",EDGE,"E0.right")])]})]});
            var Q2;
            {var subQ0=sQuery(id+"F0.wireOp",EDGE,"E0.right");var subQ1=sQuery(id+"F0.wireOp",EDGE,"E0.bottom");Q2=makeQuery(id+"F25.opFillet","TWEAK_EDGE",EDGE,{"derivedFrom":[makeQuery(id+"F2.opFillet","BLEND_VERTEX",VERTEX,{"blendedFrom":[makeQuery(id+"F1.opExtrude","CAP_VERTEX",VERTEX,{"disambiguationData":[OSD([subQ1,subQ0])],"isStart":false}),makeQuery(id+"F1.opExtrude","SWEPT_EDGE",EDGE,{"disambiguationData":[OSD([subQ1,subQ0])]}),makeQuery(id+"F1.opExtrude","CAP_EDGE",EDGE,{"disambiguationData":[OSD([subQ0])],"isStart":false}),makeQuery(id+"F1.opExtrude","SWEPT_FACE",FACE,{"disambiguationData":[OSD([subQ0])]})],"blendedInto":[makeQuery(id+"F1.opExtrude","SWEPT_FACE",FACE,{"disambiguationData":[OSD([subQ0])]})]})]});}
            var Q3;
            Q3=makeQuery(id+"F25.opFillet","BLEND_EDGE",EDGE,{"blendedFrom":[makeQuery(id+"F7.opChamfer","BLEND_EDGE",EDGE,{"blendedFrom":[makeQuery(id+"F5.opExtrude","CAP_EDGE",EDGE,{"disambiguationData":[OSD([sQuery(id+"F4.wireOp",EDGE,"E17")])],"isStart":false}),makeQuery(id+"F1.opExtrude","SWEPT_FACE",FACE,{"disambiguationData":[OSD([sQuery(id+"F0.wireOp",EDGE,"E0.bottom")])]})],"blendedInto":[makeQuery(id+"F1.opExtrude","SWEPT_FACE",FACE,{"disambiguationData":[OSD([sQuery(id+"F0.wireOp",EDGE,"E0.bottom")])]})]}),makeQuery(id+"F2.opFillet","BLEND_FACE",FACE,{"disambiguationData":[OSD([sQuery(id+"F0.wireOp",EDGE,"E0.right")])]})],"blendedInto":[makeQuery(id+"F2.opFillet","BLEND_FACE",FACE,{"disambiguationData":[OSD([sQuery(id+"F0.wireOp",EDGE,"E0.right")])]})]});
            var Q4;
            Q4=makeQuery(id+"F25.opFillet","BLEND_EDGE",EDGE,{"blendedFrom":[makeQuery(id+"F14.opChamfer","BLEND_EDGE",EDGE,{"blendedFrom":[makeQuery(id+"F5.opExtrude","CAP_EDGE",EDGE,{"disambiguationData":[OSD([sQuery(id+"F4.wireOp",EDGE,"E15")])],"isStart":false}),makeQuery(id+"F1.opExtrude","SWEPT_FACE",FACE,{"disambiguationData":[OSD([sQuery(id+"F0.wireOp",EDGE,"E0.bottom")])]})],"blendedInto":[makeQuery(id+"F1.opExtrude","SWEPT_FACE",FACE,{"disambiguationData":[OSD([sQuery(id+"F0.wireOp",EDGE,"E0.bottom")])]})]}),makeQuery(id+"F2.opFillet","BLEND_FACE",FACE,{"disambiguationData":[OSD([sQuery(id+"F0.wireOp",EDGE,"E0.left")])]})],"blendedInto":[makeQuery(id+"F2.opFillet","BLEND_FACE",FACE,{"disambiguationData":[OSD([sQuery(id+"F0.wireOp",EDGE,"E0.left")])]})]});
            var Q5;
            {var subQ0=sQuery(id+"F0.wireOp",EDGE,"E0.left");var subQ1=sQuery(id+"F0.wireOp",EDGE,"E0.bottom");Q5=makeQuery(id+"F25.opFillet","TWEAK_EDGE",EDGE,{"derivedFrom":[makeQuery(id+"F2.opFillet","BLEND_VERTEX",VERTEX,{"blendedFrom":[makeQuery(id+"F1.opExtrude","CAP_VERTEX",VERTEX,{"disambiguationData":[OSD([subQ1,subQ0])],"isStart":false}),makeQuery(id+"F1.opExtrude","SWEPT_EDGE",EDGE,{"disambiguationData":[OSD([subQ1,subQ0])]}),makeQuery(id+"F1.opExtrude","CAP_EDGE",EDGE,{"disambiguationData":[OSD([subQ0])],"isStart":false}),makeQuery(id+"F1.opExtrude","SWEPT_FACE",FACE,{"disambiguationData":[OSD([subQ0])]})],"blendedInto":[makeQuery(id+"F1.opExtrude","SWEPT_FACE",FACE,{"disambiguationData":[OSD([subQ0])]})]})]});}
            var Q6;
            Q6=makeQuery(id+"F25.opFillet","BLEND_EDGE",EDGE,{"blendedFrom":[makeQuery(id+"F13.opChamfer","BLEND_EDGE",EDGE,{"blendedFrom":[makeQuery(id+"F5.opExtrude","CAP_EDGE",EDGE,{"disambiguationData":[OSD([sQuery(id+"F4.wireOp",EDGE,"E11")])],"isStart":false}),makeQuery(id+"F1.opExtrude","SWEPT_FACE",FACE,{"disambiguationData":[OSD([sQuery(id+"F0.wireOp",EDGE,"E0.top")])]})],"blendedInto":[makeQuery(id+"F1.opExtrude","SWEPT_FACE",FACE,{"disambiguationData":[OSD([sQuery(id+"F0.wireOp",EDGE,"E0.top")])]})]}),makeQuery(id+"F2.opFillet","BLEND_FACE",FACE,{"disambiguationData":[OSD([sQuery(id+"F0.wireOp",EDGE,"E0.left")])]})],"blendedInto":[makeQuery(id+"F2.opFillet","BLEND_FACE",FACE,{"disambiguationData":[OSD([sQuery(id+"F0.wireOp",EDGE,"E0.left")])]})]});
            var Q7;
            {var subQ0=sQuery(id+"F0.wireOp",EDGE,"E0.left");var subQ1=sQuery(id+"F0.wireOp",EDGE,"E0.top");Q7=makeQuery(id+"F25.opFillet","TWEAK_EDGE",EDGE,{"derivedFrom":[makeQuery(id+"F2.opFillet","BLEND_VERTEX",VERTEX,{"blendedFrom":[makeQuery(id+"F1.opExtrude","CAP_VERTEX",VERTEX,{"disambiguationData":[OSD([subQ1,subQ0])],"isStart":false}),makeQuery(id+"F1.opExtrude","SWEPT_EDGE",EDGE,{"disambiguationData":[OSD([subQ1,subQ0])]}),makeQuery(id+"F1.opExtrude","CAP_EDGE",EDGE,{"disambiguationData":[OSD([subQ0])],"isStart":false}),makeQuery(id+"F1.opExtrude","SWEPT_FACE",FACE,{"disambiguationData":[OSD([subQ0])]})],"blendedInto":[makeQuery(id+"F1.opExtrude","SWEPT_FACE",FACE,{"disambiguationData":[OSD([subQ0])]})]})]});}
            fillet(context, id + "F26", {"entities" : qUnion([Q0, Q1, Q2, Q3, Q4, Q5, Q6, Q7]), "radius" : 1 * mm, "tangentPropagation" : true, "allowEdgeOverflow" : false});
        }
        {
            var Q0;
            {var subQ0=sQuery(id+"F4.wireOp",EDGE,"E10");Q0=makeQuery(id+"F25.opFillet","BLEND_EDGE",EDGE,{"blendedFrom":[makeQuery(id+"F15.opChamfer","BLEND_EDGE",EDGE,{"blendedFrom":[makeQuery(id+"F5.opExtrude","CAP_EDGE",EDGE,{"disambiguationData":[OSD([sQuery(id+"F4.wireOp",EDGE,"E9")])],"isStart":false}),makeQuery(id+"F1.opExtrude","SWEPT_FACE",FACE,{"disambiguationData":[OSD([sQuery(id+"F0.wireOp",EDGE,"E0.top")])]})],"blendedInto":[makeQuery(id+"F1.opExtrude","SWEPT_FACE",FACE,{"disambiguationData":[OSD([sQuery(id+"F0.wireOp",EDGE,"E0.top")])]})]}),makeQuery(id+"F9.boolean.opBoolean","MERGE",FACE,{"derivedFrom":[makeQuery(id+"F5.opExtrude","SWEPT_FACE",FACE,{"disambiguationData":[OSD([subQ0])]}),makeQuery(id+"F9.opExtrude","SWEPT_FACE",FACE,{"disambiguationData":[OSD([subQ0])]})]})],"blendedInto":[makeQuery(id+"F9.boolean.opBoolean","MERGE",FACE,{"derivedFrom":[makeQuery(id+"F5.opExtrude","SWEPT_FACE",FACE,{"disambiguationData":[OSD([subQ0])]}),makeQuery(id+"F9.opExtrude","SWEPT_FACE",FACE,{"disambiguationData":[OSD([subQ0])]})]})]});}
            var Q1;
            {var subQ0=sQuery(id+"F0.wireOp",EDGE,"E0.top");Q1=makeQuery(id+"F25.opFillet","BLEND_EDGE",EDGE,{"disambiguationData":[OD(1.0)],"blendedFrom":[makeQuery(id+"F15.opChamfer","BLEND_EDGE",EDGE,{"blendedFrom":[makeQuery(id+"F5.opExtrude","CAP_EDGE",EDGE,{"disambiguationData":[OSD([sQuery(id+"F4.wireOp",EDGE,"E9")])],"isStart":false}),makeQuery(id+"F1.opExtrude","SWEPT_FACE",FACE,{"disambiguationData":[OSD([subQ0])]})],"blendedInto":[makeQuery(id+"F1.opExtrude","SWEPT_FACE",FACE,{"disambiguationData":[OSD([subQ0])]})]}),makeQuery(id+"F24.opFillet","BLEND_FACE",FACE,{"disambiguationData":[OSD([sQuery(id+"F0.wireOp",EDGE,"E0.bottom"),subQ0,sQuery(id+"F0.wireOp",EDGE,"E0.left"),sQuery(id+"F0.wireOp",EDGE,"E0.right"),sQuery(id+"F4.wireOp",EDGE,"E3"),sQuery(id+"F4.wireOp",EDGE,"E10")])]})],"blendedInto":[makeQuery(id+"F24.opFillet","BLEND_FACE",FACE,{"disambiguationData":[OSD([sQuery(id+"F0.wireOp",EDGE,"E0.bottom"),subQ0,sQuery(id+"F0.wireOp",EDGE,"E0.left"),sQuery(id+"F0.wireOp",EDGE,"E0.right"),sQuery(id+"F4.wireOp",EDGE,"E3"),sQuery(id+"F4.wireOp",EDGE,"E10")])]})]});}
            var Q2;
            {var subQ0=sQuery(id+"F0.wireOp",EDGE,"E0.top");Q2=makeQuery(id+"F25.opFillet","BLEND_EDGE",EDGE,{"disambiguationData":[OD(1.0)],"blendedFrom":[makeQuery(id+"F13.opChamfer","BLEND_EDGE",EDGE,{"blendedFrom":[makeQuery(id+"F5.opExtrude","CAP_EDGE",EDGE,{"disambiguationData":[OSD([sQuery(id+"F4.wireOp",EDGE,"E11")])],"isStart":false}),makeQuery(id+"F1.opExtrude","SWEPT_FACE",FACE,{"disambiguationData":[OSD([subQ0])]})],"blendedInto":[makeQuery(id+"F1.opExtrude","SWEPT_FACE",FACE,{"disambiguationData":[OSD([subQ0])]})]}),makeQuery(id+"F24.opFillet","BLEND_FACE",FACE,{"disambiguationData":[OSD([sQuery(id+"F0.wireOp",EDGE,"E0.bottom"),subQ0,sQuery(id+"F0.wireOp",EDGE,"E0.left"),sQuery(id+"F0.wireOp",EDGE,"E0.right"),sQuery(id+"F4.wireOp",EDGE,"E4"),sQuery(id+"F4.wireOp",EDGE,"E12")])]})],"blendedInto":[makeQuery(id+"F24.opFillet","BLEND_FACE",FACE,{"disambiguationData":[OSD([sQuery(id+"F0.wireOp",EDGE,"E0.bottom"),subQ0,sQuery(id+"F0.wireOp",EDGE,"E0.left"),sQuery(id+"F0.wireOp",EDGE,"E0.right"),sQuery(id+"F4.wireOp",EDGE,"E4"),sQuery(id+"F4.wireOp",EDGE,"E12")])]})]});}
            var Q3;
            {var subQ0=sQuery(id+"F0.wireOp",EDGE,"E0.bottom");Q3=makeQuery(id+"F25.opFillet","BLEND_EDGE",EDGE,{"disambiguationData":[OD(1.0)],"blendedFrom":[makeQuery(id+"F14.opChamfer","BLEND_EDGE",EDGE,{"blendedFrom":[makeQuery(id+"F5.opExtrude","CAP_EDGE",EDGE,{"disambiguationData":[OSD([sQuery(id+"F4.wireOp",EDGE,"E15")])],"isStart":false}),makeQuery(id+"F1.opExtrude","SWEPT_FACE",FACE,{"disambiguationData":[OSD([subQ0])]})],"blendedInto":[makeQuery(id+"F1.opExtrude","SWEPT_FACE",FACE,{"disambiguationData":[OSD([subQ0])]})]}),makeQuery(id+"F24.opFillet","BLEND_FACE",FACE,{"disambiguationData":[OSD([subQ0,sQuery(id+"F0.wireOp",EDGE,"E0.top"),sQuery(id+"F0.wireOp",EDGE,"E0.left"),sQuery(id+"F0.wireOp",EDGE,"E0.right"),sQuery(id+"F4.wireOp",EDGE,"E4"),sQuery(id+"F4.wireOp",EDGE,"E16")])]})],"blendedInto":[makeQuery(id+"F24.opFillet","BLEND_FACE",FACE,{"disambiguationData":[OSD([subQ0,sQuery(id+"F0.wireOp",EDGE,"E0.top"),sQuery(id+"F0.wireOp",EDGE,"E0.left"),sQuery(id+"F0.wireOp",EDGE,"E0.right"),sQuery(id+"F4.wireOp",EDGE,"E4"),sQuery(id+"F4.wireOp",EDGE,"E16")])]})]});}
            var Q4;
            {var subQ0=sQuery(id+"F0.wireOp",EDGE,"E0.bottom");Q4=makeQuery(id+"F25.opFillet","BLEND_EDGE",EDGE,{"disambiguationData":[OD(1.0)],"blendedFrom":[makeQuery(id+"F7.opChamfer","BLEND_EDGE",EDGE,{"blendedFrom":[makeQuery(id+"F5.opExtrude","CAP_EDGE",EDGE,{"disambiguationData":[OSD([sQuery(id+"F4.wireOp",EDGE,"E17")])],"isStart":false}),makeQuery(id+"F1.opExtrude","SWEPT_FACE",FACE,{"disambiguationData":[OSD([subQ0])]})],"blendedInto":[makeQuery(id+"F1.opExtrude","SWEPT_FACE",FACE,{"disambiguationData":[OSD([subQ0])]})]}),makeQuery(id+"F24.opFillet","BLEND_FACE",FACE,{"disambiguationData":[OSD([subQ0,sQuery(id+"F0.wireOp",EDGE,"E0.top"),sQuery(id+"F0.wireOp",EDGE,"E0.left"),sQuery(id+"F0.wireOp",EDGE,"E0.right"),sQuery(id+"F4.wireOp",EDGE,"E3"),sQuery(id+"F4.wireOp",EDGE,"E18")])]})],"blendedInto":[makeQuery(id+"F24.opFillet","BLEND_FACE",FACE,{"disambiguationData":[OSD([subQ0,sQuery(id+"F0.wireOp",EDGE,"E0.top"),sQuery(id+"F0.wireOp",EDGE,"E0.left"),sQuery(id+"F0.wireOp",EDGE,"E0.right"),sQuery(id+"F4.wireOp",EDGE,"E3"),sQuery(id+"F4.wireOp",EDGE,"E18")])]})]});}
            fillet(context, id + "F27", {"entities" : qUnion([Q0, Q1, Q2, Q3, Q4]), "radius" : .5 * mm, "tangentPropagation" : true, "allowEdgeOverflow" : false});
        }
        {
            var Q0;
            {var subQ0=sQuery(id+"F4.wireOp",EDGE,"E14");Q0=makeQuery(id+"F25.opFillet","BLEND_EDGE",EDGE,{"blendedFrom":[makeQuery(id+"F14.opChamfer","BLEND_EDGE",EDGE,{"blendedFrom":[makeQuery(id+"F5.opExtrude","CAP_EDGE",EDGE,{"disambiguationData":[OSD([sQuery(id+"F4.wireOp",EDGE,"E15")])],"isStart":false}),makeQuery(id+"F1.opExtrude","SWEPT_FACE",FACE,{"disambiguationData":[OSD([sQuery(id+"F0.wireOp",EDGE,"E0.bottom")])]})],"blendedInto":[makeQuery(id+"F1.opExtrude","SWEPT_FACE",FACE,{"disambiguationData":[OSD([sQuery(id+"F0.wireOp",EDGE,"E0.bottom")])]})]}),makeQuery(id+"F9.boolean.opBoolean","MERGE",FACE,{"derivedFrom":[makeQuery(id+"F5.opExtrude","SWEPT_FACE",FACE,{"disambiguationData":[OSD([subQ0])]}),makeQuery(id+"F9.opExtrude","SWEPT_FACE",FACE,{"disambiguationData":[OSD([subQ0])]})]})],"blendedInto":[makeQuery(id+"F9.boolean.opBoolean","MERGE",FACE,{"derivedFrom":[makeQuery(id+"F5.opExtrude","SWEPT_FACE",FACE,{"disambiguationData":[OSD([subQ0])]}),makeQuery(id+"F9.opExtrude","SWEPT_FACE",FACE,{"disambiguationData":[OSD([subQ0])]})]})]});}
            var Q1;
            {var subQ0=sQuery(id+"F4.wireOp",EDGE,"E13");Q1=makeQuery(id+"F25.opFillet","BLEND_EDGE",EDGE,{"blendedFrom":[makeQuery(id+"F7.opChamfer","BLEND_EDGE",EDGE,{"blendedFrom":[makeQuery(id+"F5.opExtrude","CAP_EDGE",EDGE,{"disambiguationData":[OSD([sQuery(id+"F4.wireOp",EDGE,"E17")])],"isStart":false}),makeQuery(id+"F1.opExtrude","SWEPT_FACE",FACE,{"disambiguationData":[OSD([sQuery(id+"F0.wireOp",EDGE,"E0.bottom")])]})],"blendedInto":[makeQuery(id+"F1.opExtrude","SWEPT_FACE",FACE,{"disambiguationData":[OSD([sQuery(id+"F0.wireOp",EDGE,"E0.bottom")])]})]}),makeQuery(id+"F6.boolean.opBoolean","MERGE",FACE,{"derivedFrom":[makeQuery(id+"F5.opExtrude","SWEPT_FACE",FACE,{"disambiguationData":[OSD([subQ0])]}),makeQuery(id+"F6.opExtrude","SWEPT_FACE",FACE,{"disambiguationData":[OSD([subQ0])]})]})],"blendedInto":[makeQuery(id+"F6.boolean.opBoolean","MERGE",FACE,{"derivedFrom":[makeQuery(id+"F5.opExtrude","SWEPT_FACE",FACE,{"disambiguationData":[OSD([subQ0])]}),makeQuery(id+"F6.opExtrude","SWEPT_FACE",FACE,{"disambiguationData":[OSD([subQ0])]})]})]});}
            var Q2;
            {var subQ0=sQuery(id+"F4.wireOp",EDGE,"E7");Q2=makeQuery(id+"F25.opFillet","BLEND_EDGE",EDGE,{"blendedFrom":[makeQuery(id+"F15.opChamfer","BLEND_EDGE",EDGE,{"blendedFrom":[makeQuery(id+"F5.opExtrude","CAP_EDGE",EDGE,{"disambiguationData":[OSD([sQuery(id+"F4.wireOp",EDGE,"E9")])],"isStart":false}),makeQuery(id+"F1.opExtrude","SWEPT_FACE",FACE,{"disambiguationData":[OSD([sQuery(id+"F0.wireOp",EDGE,"E0.top")])]})],"blendedInto":[makeQuery(id+"F1.opExtrude","SWEPT_FACE",FACE,{"disambiguationData":[OSD([sQuery(id+"F0.wireOp",EDGE,"E0.top")])]})]}),makeQuery(id+"F9.boolean.opBoolean","MERGE",FACE,{"derivedFrom":[makeQuery(id+"F5.opExtrude","SWEPT_FACE",FACE,{"disambiguationData":[OSD([subQ0])]}),makeQuery(id+"F9.opExtrude","SWEPT_FACE",FACE,{"disambiguationData":[OSD([subQ0])]})]})],"blendedInto":[makeQuery(id+"F9.boolean.opBoolean","MERGE",FACE,{"derivedFrom":[makeQuery(id+"F5.opExtrude","SWEPT_FACE",FACE,{"disambiguationData":[OSD([subQ0])]}),makeQuery(id+"F9.opExtrude","SWEPT_FACE",FACE,{"disambiguationData":[OSD([subQ0])]})]})]});}
            var Q3;
            {var subQ0=sQuery(id+"F4.wireOp",EDGE,"E8");Q3=makeQuery(id+"F25.opFillet","BLEND_EDGE",EDGE,{"blendedFrom":[makeQuery(id+"F13.opChamfer","BLEND_EDGE",EDGE,{"blendedFrom":[makeQuery(id+"F5.opExtrude","CAP_EDGE",EDGE,{"disambiguationData":[OSD([sQuery(id+"F4.wireOp",EDGE,"E11")])],"isStart":false}),makeQuery(id+"F1.opExtrude","SWEPT_FACE",FACE,{"disambiguationData":[OSD([sQuery(id+"F0.wireOp",EDGE,"E0.top")])]})],"blendedInto":[makeQuery(id+"F1.opExtrude","SWEPT_FACE",FACE,{"disambiguationData":[OSD([sQuery(id+"F0.wireOp",EDGE,"E0.top")])]})]}),makeQuery(id+"F9.boolean.opBoolean","MERGE",FACE,{"derivedFrom":[makeQuery(id+"F5.opExtrude","SWEPT_FACE",FACE,{"disambiguationData":[OSD([subQ0])]}),makeQuery(id+"F9.opExtrude","SWEPT_FACE",FACE,{"disambiguationData":[OSD([subQ0])]})]})],"blendedInto":[makeQuery(id+"F9.boolean.opBoolean","MERGE",FACE,{"derivedFrom":[makeQuery(id+"F5.opExtrude","SWEPT_FACE",FACE,{"disambiguationData":[OSD([subQ0])]}),makeQuery(id+"F9.opExtrude","SWEPT_FACE",FACE,{"disambiguationData":[OSD([subQ0])]})]})]});}
            fillet(context, id + "F28", {"entities" : qUnion([Q0, Q1, Q2, Q3]), "radius" : .5 * mm, "tangentPropagation" : true, "allowEdgeOverflow" : false});
        }
        {
            var Q0;
            {var subQ0=sQuery(id+"F0.wireOp",EDGE,"E0.right");var subQ1=sQuery(id+"F0.wireOp",EDGE,"E0.top");Q0=makeQuery(id+"F24.opFillet","BLEND_EDGE",EDGE,{"blendedFrom":[makeQuery(id+"F5.boolean.opBoolean","MERGE",EDGE,{"derivedFrom":[makeQuery(id+"F2.opFillet","BLEND_EDGE",EDGE,{"blendedFrom":[makeQuery(id+"F1.opExtrude","SWEPT_EDGE",EDGE,{"disambiguationData":[OSD([subQ1,subQ0])]}),makeQuery(id+"F1.opExtrude","SWEPT_FACE",FACE,{"disambiguationData":[OSD([subQ1])]})],"blendedInto":[makeQuery(id+"F1.opExtrude","SWEPT_FACE",FACE,{"disambiguationData":[OSD([subQ1])]})]}),makeQuery(id+"F5.opExtrude","SWEPT_EDGE",EDGE,{"disambiguationData":[OSD([sQuery(id+"F0.wireOp",EDGE,"E0.bottom"),subQ1,sQuery(id+"F0.wireOp",EDGE,"E0.left"),subQ0,sQuery(id+"F4.wireOp",EDGE,"E3"),sQuery(id+"F4.wireOp",EDGE,"E10")])]})]}),makeQuery(id+"F11.opChamfer","BLEND_FACE",FACE,{"disambiguationData":[OSD([sQuery(id+"F8.wireOp",EDGE,"E20")])]})],"blendedInto":[makeQuery(id+"F11.opChamfer","BLEND_FACE",FACE,{"disambiguationData":[OSD([sQuery(id+"F8.wireOp",EDGE,"E20")])]})]});}
            var Q1;
            {var subQ0=sQuery(id+"F4.wireOp",EDGE,"E10");Q1=makeQuery(id+"F11.opChamfer","BLEND_EDGE",EDGE,{"blendedFrom":[makeQuery(id+"F9.opExtrude","CAP_EDGE",EDGE,{"disambiguationData":[OSD([sQuery(id+"F8.wireOp",EDGE,"E20")])],"isStart":false}),makeQuery(id+"F9.boolean.opBoolean","MERGE",FACE,{"derivedFrom":[makeQuery(id+"F5.opExtrude","SWEPT_FACE",FACE,{"disambiguationData":[OSD([subQ0])]}),makeQuery(id+"F9.opExtrude","SWEPT_FACE",FACE,{"disambiguationData":[OSD([subQ0])]})]})],"blendedInto":[makeQuery(id+"F9.boolean.opBoolean","MERGE",FACE,{"derivedFrom":[makeQuery(id+"F5.opExtrude","SWEPT_FACE",FACE,{"disambiguationData":[OSD([subQ0])]}),makeQuery(id+"F9.opExtrude","SWEPT_FACE",FACE,{"disambiguationData":[OSD([subQ0])]})]})]});}
            var Q2;
            {var subQ0=sQuery(id+"F0.wireOp",EDGE,"E0.left");var subQ1=sQuery(id+"F0.wireOp",EDGE,"E0.top");Q2=makeQuery(id+"F24.opFillet","BLEND_EDGE",EDGE,{"blendedFrom":[makeQuery(id+"F5.boolean.opBoolean","MERGE",EDGE,{"derivedFrom":[makeQuery(id+"F2.opFillet","BLEND_EDGE",EDGE,{"blendedFrom":[makeQuery(id+"F1.opExtrude","SWEPT_EDGE",EDGE,{"disambiguationData":[OSD([subQ1,subQ0])]}),makeQuery(id+"F1.opExtrude","SWEPT_FACE",FACE,{"disambiguationData":[OSD([subQ1])]})],"blendedInto":[makeQuery(id+"F1.opExtrude","SWEPT_FACE",FACE,{"disambiguationData":[OSD([subQ1])]})]}),makeQuery(id+"F5.opExtrude","SWEPT_EDGE",EDGE,{"disambiguationData":[OSD([sQuery(id+"F0.wireOp",EDGE,"E0.bottom"),subQ1,subQ0,sQuery(id+"F0.wireOp",EDGE,"E0.right"),sQuery(id+"F4.wireOp",EDGE,"E4"),sQuery(id+"F4.wireOp",EDGE,"E12")])]})]}),makeQuery(id+"F11.opChamfer","BLEND_FACE",FACE,{"disambiguationData":[OSD([sQuery(id+"F8.wireOp",EDGE,"E21")])]})],"blendedInto":[makeQuery(id+"F11.opChamfer","BLEND_FACE",FACE,{"disambiguationData":[OSD([sQuery(id+"F8.wireOp",EDGE,"E21")])]})]});}
            var Q3;
            {var subQ0=sQuery(id+"F4.wireOp",EDGE,"E12");Q3=makeQuery(id+"F11.opChamfer","BLEND_EDGE",EDGE,{"blendedFrom":[makeQuery(id+"F9.opExtrude","CAP_EDGE",EDGE,{"disambiguationData":[OSD([sQuery(id+"F8.wireOp",EDGE,"E21")])],"isStart":false}),makeQuery(id+"F9.boolean.opBoolean","MERGE",FACE,{"derivedFrom":[makeQuery(id+"F5.opExtrude","SWEPT_FACE",FACE,{"disambiguationData":[OSD([subQ0])]}),makeQuery(id+"F9.opExtrude","SWEPT_FACE",FACE,{"disambiguationData":[OSD([subQ0])]})]})],"blendedInto":[makeQuery(id+"F9.boolean.opBoolean","MERGE",FACE,{"derivedFrom":[makeQuery(id+"F5.opExtrude","SWEPT_FACE",FACE,{"disambiguationData":[OSD([subQ0])]}),makeQuery(id+"F9.opExtrude","SWEPT_FACE",FACE,{"disambiguationData":[OSD([subQ0])]})]})]});}
            var Q4;
            {var subQ0=sQuery(id+"F0.wireOp",EDGE,"E0.left");var subQ1=sQuery(id+"F0.wireOp",EDGE,"E0.bottom");Q4=makeQuery(id+"F24.opFillet","BLEND_EDGE",EDGE,{"blendedFrom":[makeQuery(id+"F5.boolean.opBoolean","MERGE",EDGE,{"derivedFrom":[makeQuery(id+"F2.opFillet","BLEND_EDGE",EDGE,{"blendedFrom":[makeQuery(id+"F1.opExtrude","SWEPT_EDGE",EDGE,{"disambiguationData":[OSD([subQ1,subQ0])]}),makeQuery(id+"F1.opExtrude","SWEPT_FACE",FACE,{"disambiguationData":[OSD([subQ1])]})],"blendedInto":[makeQuery(id+"F1.opExtrude","SWEPT_FACE",FACE,{"disambiguationData":[OSD([subQ1])]})]}),makeQuery(id+"F5.opExtrude","SWEPT_EDGE",EDGE,{"disambiguationData":[OSD([subQ1,sQuery(id+"F0.wireOp",EDGE,"E0.top"),subQ0,sQuery(id+"F0.wireOp",EDGE,"E0.right"),sQuery(id+"F4.wireOp",EDGE,"E4"),sQuery(id+"F4.wireOp",EDGE,"E16")])]})]}),makeQuery(id+"F12.opChamfer","BLEND_FACE",FACE,{"disambiguationData":[OSD([sQuery(id+"F8.wireOp",EDGE,"E19")])]})],"blendedInto":[makeQuery(id+"F12.opChamfer","BLEND_FACE",FACE,{"disambiguationData":[OSD([sQuery(id+"F8.wireOp",EDGE,"E19")])]})]});}
            var Q5;
            {var subQ0=sQuery(id+"F4.wireOp",EDGE,"E16");Q5=makeQuery(id+"F12.opChamfer","BLEND_EDGE",EDGE,{"blendedFrom":[makeQuery(id+"F9.opExtrude","CAP_EDGE",EDGE,{"disambiguationData":[OSD([sQuery(id+"F8.wireOp",EDGE,"E19")])],"isStart":false}),makeQuery(id+"F9.boolean.opBoolean","MERGE",FACE,{"derivedFrom":[makeQuery(id+"F5.opExtrude","SWEPT_FACE",FACE,{"disambiguationData":[OSD([subQ0])]}),makeQuery(id+"F9.opExtrude","SWEPT_FACE",FACE,{"disambiguationData":[OSD([subQ0])]})]})],"blendedInto":[makeQuery(id+"F9.boolean.opBoolean","MERGE",FACE,{"derivedFrom":[makeQuery(id+"F5.opExtrude","SWEPT_FACE",FACE,{"disambiguationData":[OSD([subQ0])]}),makeQuery(id+"F9.opExtrude","SWEPT_FACE",FACE,{"disambiguationData":[OSD([subQ0])]})]})]});}
            var Q6;
            {var subQ0=sQuery(id+"F0.wireOp",EDGE,"E0.bottom");var subQ1=sQuery(id+"F0.wireOp",EDGE,"E0.right");Q6=makeQuery(id+"F24.opFillet","BLEND_EDGE",EDGE,{"blendedFrom":[makeQuery(id+"F5.boolean.opBoolean","MERGE",EDGE,{"derivedFrom":[makeQuery(id+"F2.opFillet","BLEND_EDGE",EDGE,{"blendedFrom":[makeQuery(id+"F1.opExtrude","SWEPT_EDGE",EDGE,{"disambiguationData":[OSD([subQ0,subQ1])]}),makeQuery(id+"F1.opExtrude","SWEPT_FACE",FACE,{"disambiguationData":[OSD([subQ0])]})],"blendedInto":[makeQuery(id+"F1.opExtrude","SWEPT_FACE",FACE,{"disambiguationData":[OSD([subQ0])]})]}),makeQuery(id+"F5.opExtrude","SWEPT_EDGE",EDGE,{"disambiguationData":[OSD([subQ0,sQuery(id+"F0.wireOp",EDGE,"E0.top"),sQuery(id+"F0.wireOp",EDGE,"E0.left"),subQ1,sQuery(id+"F4.wireOp",EDGE,"E3"),sQuery(id+"F4.wireOp",EDGE,"E18")])]})]}),makeQuery(id+"F10.opChamfer","BLEND_FACE",FACE,{"disambiguationData":[OSD([subQ0])]})],"blendedInto":[makeQuery(id+"F10.opChamfer","BLEND_FACE",FACE,{"disambiguationData":[OSD([subQ0])]})]});}
            var Q7;
            {var subQ0=sQuery(id+"F4.wireOp",EDGE,"E18");Q7=makeQuery(id+"F10.opChamfer","BLEND_EDGE",EDGE,{"blendedFrom":[makeQuery(id+"F6.opExtrude","CAP_EDGE",EDGE,{"disambiguationData":[OSD([sQuery(id+"F0.wireOp",EDGE,"E0.bottom")])],"isStart":false}),makeQuery(id+"F6.boolean.opBoolean","MERGE",FACE,{"derivedFrom":[makeQuery(id+"F5.opExtrude","SWEPT_FACE",FACE,{"disambiguationData":[OSD([subQ0])]}),makeQuery(id+"F6.opExtrude","SWEPT_FACE",FACE,{"disambiguationData":[OSD([subQ0])]})]})],"blendedInto":[makeQuery(id+"F6.boolean.opBoolean","MERGE",FACE,{"derivedFrom":[makeQuery(id+"F5.opExtrude","SWEPT_FACE",FACE,{"disambiguationData":[OSD([subQ0])]}),makeQuery(id+"F6.opExtrude","SWEPT_FACE",FACE,{"disambiguationData":[OSD([subQ0])]})]})]});}
            fillet(context, id + "F29", {"entities" : qUnion([Q0, Q1, Q2, Q3, Q4, Q5, Q6, Q7]), "radius" : .5 * mm, "allowEdgeOverflow" : false});
        }
        {
            var Q0;
            {var subQ0=sQuery(id+"F4.wireOp",EDGE,"E16");var subQ1=sQuery(id+"F4.wireOp",EDGE,"E15");Q0=makeQuery(id+"F9.boolean.opBoolean","MERGE",EDGE,{"derivedFrom":[makeQuery(id+"F5.opExtrude","SWEPT_EDGE",EDGE,{"disambiguationData":[OSD([subQ1,subQ0])]}),makeQuery(id+"F9.opExtrude","SWEPT_EDGE",EDGE,{"disambiguationData":[OSD([subQ1,subQ0])]})]});}
            var Q1;
            {var subQ0=sQuery(id+"F4.wireOp",EDGE,"E18");var subQ1=sQuery(id+"F4.wireOp",EDGE,"E17");Q1=makeQuery(id+"F6.boolean.opBoolean","MERGE",EDGE,{"derivedFrom":[makeQuery(id+"F5.opExtrude","SWEPT_EDGE",EDGE,{"disambiguationData":[OSD([subQ1,subQ0])]}),makeQuery(id+"F6.opExtrude","SWEPT_EDGE",EDGE,{"disambiguationData":[OSD([subQ1,subQ0])]})]});}
            var Q2;
            {var subQ0=sQuery(id+"F4.wireOp",EDGE,"E9");var subQ1=sQuery(id+"F4.wireOp",EDGE,"E7");Q2=makeQuery(id+"F9.boolean.opBoolean","MERGE",EDGE,{"derivedFrom":[makeQuery(id+"F5.opExtrude","SWEPT_EDGE",EDGE,{"disambiguationData":[OSD([subQ1,subQ0])]}),makeQuery(id+"F9.opExtrude","SWEPT_EDGE",EDGE,{"disambiguationData":[OSD([subQ1,subQ0])]})]});}
            var Q3;
            {var subQ0=sQuery(id+"F4.wireOp",EDGE,"E12");var subQ1=sQuery(id+"F4.wireOp",EDGE,"E11");Q3=makeQuery(id+"F9.boolean.opBoolean","MERGE",EDGE,{"derivedFrom":[makeQuery(id+"F5.opExtrude","SWEPT_EDGE",EDGE,{"disambiguationData":[OSD([subQ1,subQ0])]}),makeQuery(id+"F9.opExtrude","SWEPT_EDGE",EDGE,{"disambiguationData":[OSD([subQ1,subQ0])]})]});}
            fillet(context, id + "F30", {"entities" : qUnion([Q0, Q1, Q2, Q3]), "radius" : .7 * mm, "tangentPropagation" : true, "allowEdgeOverflow" : false});
        }
    });
